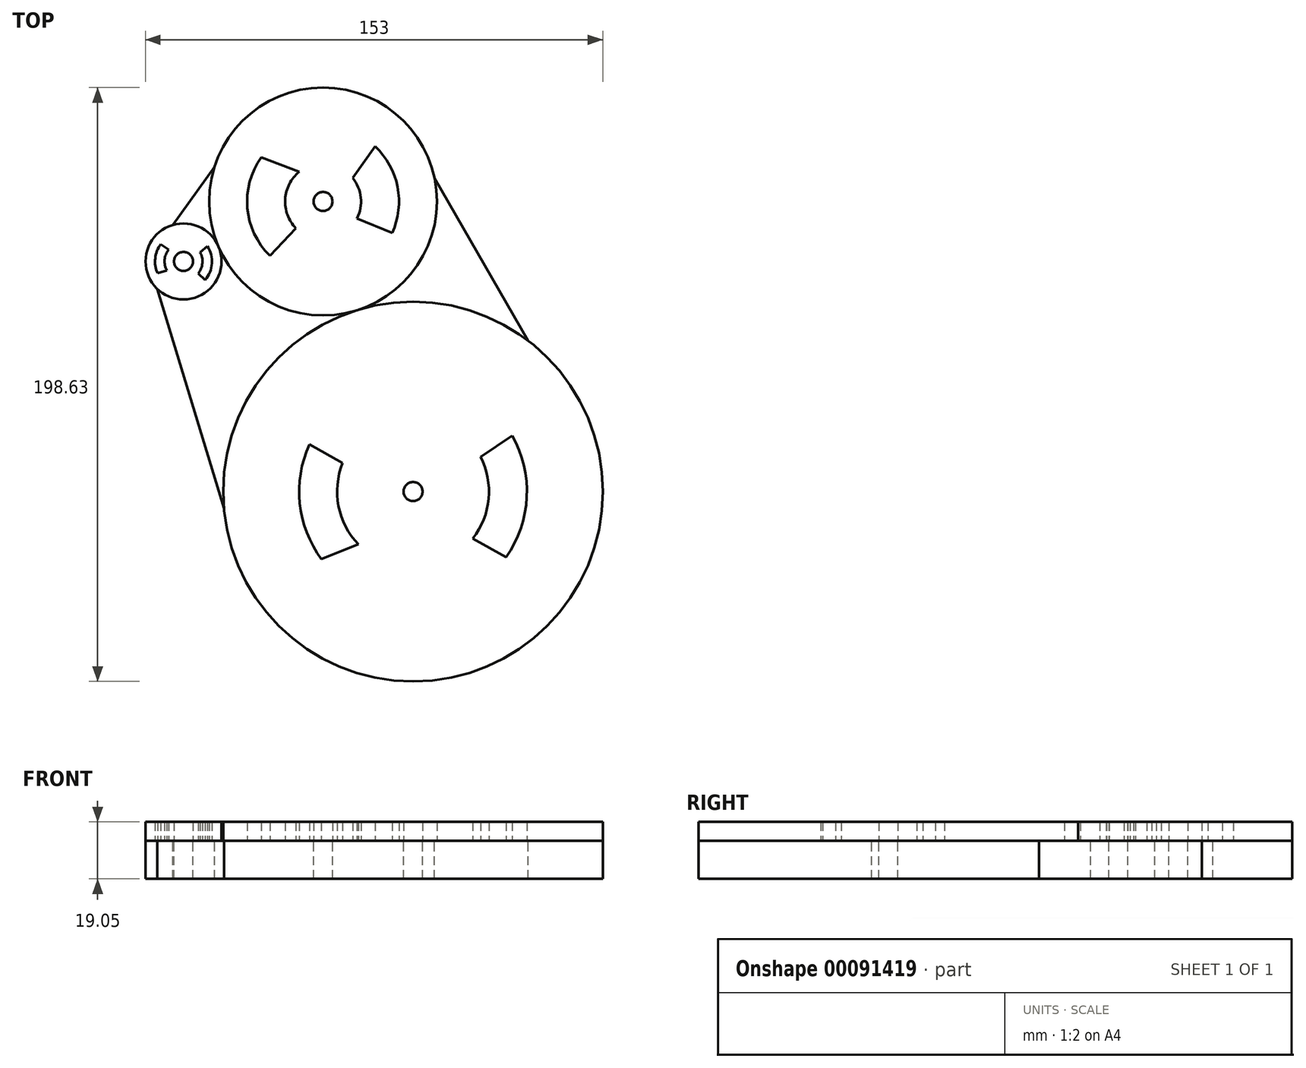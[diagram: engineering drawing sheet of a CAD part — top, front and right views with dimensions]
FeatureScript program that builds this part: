
annotation { "Feature Type Name" : "Feature", "Feature Type Description" : "" }
export const myFeature = defineFeature(function(context is Context, id is Id, definition is map)
    precondition{}
    {
        {
            var Q0;
            Q0=qCreatedBy(makeId("Top.planeOp"),FACE);
            var sketch = newSketch(context, id + "F0", { "sketchPlane" : qUnion([Q0])});
            skCircle(sketch, "E0", {"center": v(-46.14, 26.52) * mm, "radius": 12.7 * mm});
            skCircle(sketch, "E1", {"center": v(0.54, 46.56) * mm, "radius": 38.1 * mm});
            skLineSegment(sketch, "E2", {"start": v(-46.14, 26.52) * mm, "end": v(0.54, 46.56) * mm, "construction": true});
            skCircle(sketch, "E3", {"center": v(30.66, -50.47) * mm, "radius": 63.5 * mm});
            skLineSegment(sketch, "E4", {"start": v(0.54, 46.56) * mm, "end": v(30.66, -50.47) * mm, "construction": true});
            skCircle(sketch, "E5", {"center": v(30.66, -50.47) * mm, "radius": 3.18 * mm});
            skCircle(sketch, "E6", {"center": v(0.54, 46.56) * mm, "radius": 3.18 * mm});
            skCircle(sketch, "E7", {"center": v(-46.14, 26.52) * mm, "radius": 3.18 * mm});
            skLineSegment(sketch, "E8", {"start": v(-54.86, 17.28) * mm, "end": v(-32.6, -56.1) * mm});
            skLineSegment(sketch, "E9", {"start": v(37.8, 54.52) * mm, "end": v(69.2, 0) * mm});
            skLineSegment(sketch, "E10", {"start": v(-49.74, 38.7) * mm, "end": v(-35.75, 58.17) * mm});
            skCircle(sketch, "E11", {"center": v(30.66, -50.47) * mm, "radius": 25.4 * mm});
            skCircle(sketch, "E12", {"center": v(30.66, -50.47) * mm, "radius": 38.1 * mm});
            skLineSegment(sketch, "E13", {"start": v(7.11, -40.94) * mm, "end": v(-4.01, -34.67) * mm});
            skLineSegment(sketch, "E14", {"start": v(12.4, -68.13) * mm, "end": v(0, -73.09) * mm});
            skLineSegment(sketch, "E15", {"start": v(50.66, -66.13) * mm, "end": v(61.8, -72.4) * mm});
            skLineSegment(sketch, "E16", {"start": v(53.25, -38.86) * mm, "end": v(63.82, -31.7) * mm});
            skCircle(sketch, "E17", {"center": v(0.54, 46.56) * mm, "radius": 12.7 * mm});
            skCircle(sketch, "E18", {"center": v(0.54, 46.56) * mm, "radius": 25.4 * mm});
            skLineSegment(sketch, "E19", {"start": v(-7.38, 56.5) * mm, "end": v(-20.13, 61.33) * mm});
            skLineSegment(sketch, "E20", {"start": v(-8.5, 37.64) * mm, "end": v(-17.23, 28.41) * mm});
            skLineSegment(sketch, "E21", {"start": v(11.9, 40.9) * mm, "end": v(23.63, 36) * mm});
            skLineSegment(sketch, "E22", {"start": v(10.47, 54.48) * mm, "end": v(18, 65) * mm});
            skCircle(sketch, "E23", {"center": v(-46.14, 26.52) * mm, "radius": 6.35 * mm});
            skCircle(sketch, "E24", {"center": v(-46.14, 26.52) * mm, "radius": 9.53 * mm});
            skLineSegment(sketch, "E25", {"start": v(-51.1, 30.48) * mm, "end": v(-53.72, 32.28) * mm});
            skLineSegment(sketch, "E26", {"start": v(-51.7, 23.44) * mm, "end": v(-54.8, 22.55) * mm});
            skLineSegment(sketch, "E27", {"start": v(-41.23, 22.5) * mm, "end": v(-38.9, 20.32) * mm});
            skLineSegment(sketch, "E28", {"start": v(-40.6, 29.63) * mm, "end": v(-38.1, 31.63) * mm});
            skSolve(sketch);
        }
        {
            var Q0;
            Q0=makeQuery(id+"F0.imprint","IMPRINT",FACE,{"disambiguationData":[TD([[makeQuery(id+"F0.imprint","IMPRINT",EDGE,{"derivedFrom":sQuery(id+"F0.wireOp",EDGE,"E6")}),-1.0]])]});
            var Q1;
            Q1=makeQuery(id+"F0.imprint","IMPRINT",FACE,{"disambiguationData":[TD([[makeQuery(id+"F0.imprint","IMPRINT",EDGE,{"derivedFrom":sQuery(id+"F0.wireOp",EDGE,"E3")}),1.0]])]});
            var Q2;
            Q2=makeQuery(id+"F0.imprint","IMPRINT",FACE,{"disambiguationData":[TD([[makeQuery(id+"F0.imprint","IMPRINT",EDGE,{"derivedFrom":sQuery(id+"F0.wireOp",EDGE,"E0")}),1.0]])]});
            var Q3;
            {var subQ0=sQuery(id+"F0.wireOp",EDGE,"E13");Q3=makeQuery(id+"F0.imprint","IMPRINT",FACE,{"disambiguationData":[TD([[makeQuery(id+"F0.imprint","IMPRINT",EDGE,{"derivedFrom":subQ0}),-1.0]])]});}
            var Q4;
            Q4=makeQuery(id+"F0.imprint","IMPRINT",FACE,{"disambiguationData":[TD([[makeQuery(id+"F0.imprint","IMPRINT",EDGE,{"derivedFrom":sQuery(id+"F0.wireOp",EDGE,"E5")}),-1.0]])]});
            var Q5;
            {var subQ0=sQuery(id+"F0.wireOp",EDGE,"E14");Q5=makeQuery(id+"F0.imprint","IMPRINT",FACE,{"disambiguationData":[TD([[makeQuery(id+"F0.imprint","IMPRINT",EDGE,{"derivedFrom":subQ0}),1.0]])]});}
            var Q6;
            {var subQ0=sQuery(id+"F0.wireOp",EDGE,"E19");Q6=makeQuery(id+"F0.imprint","IMPRINT",FACE,{"disambiguationData":[TD([[makeQuery(id+"F0.imprint","IMPRINT",EDGE,{"derivedFrom":subQ0}),-1.0]])]});}
            var Q7;
            {var subQ0=sQuery(id+"F0.wireOp",EDGE,"E1");var subQ1=makeQuery(id+"F0.imprint","INTERSECT",VERTEX,{"derivedFrom":[subQ0,sQuery(id+"F0.wireOp",EDGE,"E9")]});Q7=makeQuery(id+"F0.imprint","IMPRINT",FACE,{"disambiguationData":[TD([[makeQuery(id+"F0.imprint","IMPRINT",EDGE,{"disambiguationData":[TD([[subQ1,-1.0]])],"derivedFrom":subQ0}),1.0]])]});}
            var Q8;
            {var subQ0=sQuery(id+"F0.wireOp",EDGE,"E20");Q8=makeQuery(id+"F0.imprint","IMPRINT",FACE,{"disambiguationData":[TD([[makeQuery(id+"F0.imprint","IMPRINT",EDGE,{"derivedFrom":subQ0}),1.0]])]});}
            var Q9;
            Q9=makeQuery(id+"F0.imprint","IMPRINT",FACE,{"disambiguationData":[TD([[makeQuery(id+"F0.imprint","IMPRINT",EDGE,{"derivedFrom":sQuery(id+"F0.wireOp",EDGE,"E7")}),-1.0]])]});
            var Q10;
            {var subQ0=sQuery(id+"F0.wireOp",EDGE,"E26");Q10=makeQuery(id+"F0.imprint","IMPRINT",FACE,{"disambiguationData":[TD([[makeQuery(id+"F0.imprint","IMPRINT",EDGE,{"derivedFrom":subQ0}),1.0]])]});}
            var Q11;
            {var subQ0=sQuery(id+"F0.wireOp",EDGE,"E25");Q11=makeQuery(id+"F0.imprint","IMPRINT",FACE,{"disambiguationData":[TD([[makeQuery(id+"F0.imprint","IMPRINT",EDGE,{"derivedFrom":subQ0}),-1.0]])]});}
            extrude(context, id + "F1", {"entities" : qUnion([Q0, Q1, Q2, Q3, Q4, Q5, Q6, Q7, Q8, Q9, Q10, Q11]), "depth" : 6.35 * mm});
        }
        {
            var Q0;
            Q0 = qSketchRegion(id + "F0", true);
            var Q1;
            {var subQ0=sQuery(id+"F0.wireOp",EDGE,"E14");Q1=makeQuery(id+"F0.imprint","IMPRINT",FACE,{"disambiguationData":[TD([[makeQuery(id+"F0.imprint","IMPRINT",EDGE,{"derivedFrom":subQ0}),1.0]])]});}
            var Q2;
            Q2=makeQuery(id+"F0.imprint","IMPRINT",FACE,{"disambiguationData":[TD([[makeQuery(id+"F0.imprint","IMPRINT",EDGE,{"derivedFrom":sQuery(id+"F0.wireOp",EDGE,"E5")}),-1.0]])]});
            var Q3;
            {var subQ0=sQuery(id+"F0.wireOp",EDGE,"E13");Q3=makeQuery(id+"F0.imprint","IMPRINT",FACE,{"disambiguationData":[TD([[makeQuery(id+"F0.imprint","IMPRINT",EDGE,{"derivedFrom":subQ0}),-1.0]])]});}
            var Q4;
            {var subQ0=sQuery(id+"F0.wireOp",EDGE,"E15");Q4=makeQuery(id+"F0.imprint","IMPRINT",FACE,{"disambiguationData":[TD([[makeQuery(id+"F0.imprint","IMPRINT",EDGE,{"derivedFrom":subQ0}),1.0]])]});}
            var Q5;
            {var subQ0=sQuery(id+"F0.wireOp",EDGE,"E13");Q5=makeQuery(id+"F0.imprint","IMPRINT",FACE,{"disambiguationData":[TD([[makeQuery(id+"F0.imprint","IMPRINT",EDGE,{"derivedFrom":subQ0}),1.0]])]});}
            var Q6;
            {var subQ0=sQuery(id+"F0.wireOp",EDGE,"E20");Q6=makeQuery(id+"F0.imprint","IMPRINT",FACE,{"disambiguationData":[TD([[makeQuery(id+"F0.imprint","IMPRINT",EDGE,{"derivedFrom":subQ0}),1.0]])]});}
            var Q7;
            Q7=makeQuery(id+"F0.imprint","IMPRINT",FACE,{"disambiguationData":[TD([[makeQuery(id+"F0.imprint","IMPRINT",EDGE,{"derivedFrom":sQuery(id+"F0.wireOp",EDGE,"E6")}),-1.0]])]});
            var Q8;
            {var subQ0=sQuery(id+"F0.wireOp",EDGE,"E19");Q8=makeQuery(id+"F0.imprint","IMPRINT",FACE,{"disambiguationData":[TD([[makeQuery(id+"F0.imprint","IMPRINT",EDGE,{"derivedFrom":subQ0}),-1.0]])]});}
            var Q9;
            {var subQ0=sQuery(id+"F0.wireOp",EDGE,"E21");Q9=makeQuery(id+"F0.imprint","IMPRINT",FACE,{"disambiguationData":[TD([[makeQuery(id+"F0.imprint","IMPRINT",EDGE,{"derivedFrom":subQ0}),1.0]])]});}
            var Q10;
            {var subQ0=sQuery(id+"F0.wireOp",EDGE,"E19");Q10=makeQuery(id+"F0.imprint","IMPRINT",FACE,{"disambiguationData":[TD([[makeQuery(id+"F0.imprint","IMPRINT",EDGE,{"derivedFrom":subQ0}),1.0]])]});}
            var Q11;
            {var subQ0=sQuery(id+"F0.wireOp",EDGE,"E25");Q11=makeQuery(id+"F0.imprint","IMPRINT",FACE,{"disambiguationData":[TD([[makeQuery(id+"F0.imprint","IMPRINT",EDGE,{"derivedFrom":subQ0}),-1.0]])]});}
            var Q12;
            {var subQ0=sQuery(id+"F0.wireOp",EDGE,"E27");Q12=makeQuery(id+"F0.imprint","IMPRINT",FACE,{"disambiguationData":[TD([[makeQuery(id+"F0.imprint","IMPRINT",EDGE,{"derivedFrom":subQ0}),1.0]])]});}
            var Q13;
            {var subQ0=sQuery(id+"F0.wireOp",EDGE,"E25");Q13=makeQuery(id+"F0.imprint","IMPRINT",FACE,{"disambiguationData":[TD([[makeQuery(id+"F0.imprint","IMPRINT",EDGE,{"derivedFrom":subQ0}),1.0]])]});}
            var Q14;
            {var subQ0=sQuery(id+"F0.wireOp",EDGE,"E26");Q14=makeQuery(id+"F0.imprint","IMPRINT",FACE,{"disambiguationData":[TD([[makeQuery(id+"F0.imprint","IMPRINT",EDGE,{"derivedFrom":subQ0}),1.0]])]});}
            var Q15;
            Q15=makeQuery(id+"F0.imprint","IMPRINT",FACE,{"disambiguationData":[TD([[makeQuery(id+"F0.imprint","IMPRINT",EDGE,{"derivedFrom":sQuery(id+"F0.wireOp",EDGE,"E7")}),-1.0]])]});
            extrude(context, id + "F2", {"entities" : qUnion([Q0, Q1, Q2, Q3, Q4, Q5, Q6, Q7, Q8, Q9, Q10, Q11, Q12, Q13, Q14, Q15]), "oppositeDirection" : true, "depth" : 12.7 * mm});
        }
    });
